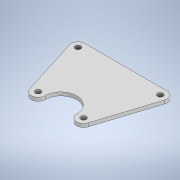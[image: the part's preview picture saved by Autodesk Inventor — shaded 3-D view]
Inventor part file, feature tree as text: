
AUTODESK INVENTOR PART (.ipt)
format: ipt  version: 2020 (Build 240168000, 168)  size: 121,856 bytes
history: native  units: in
note: dims shown in document units (in); Inventor stores cm internally (conversion verified against a paired STEP export)
features: extrude x1, sketch x1
ambient origin geometry x8: Origin, YZ Plane, XZ Plane, XY Plane, X Axis, Y Axis, Z Axis, Center Point
bodies: Solid1 (feature_tree)
feature tree (2):
  extrude  "Extrusion1"  Depth=0.0787in
  sketch  "Sketch1"  dims[d0=1.8898in d1=1.3386in d2=0.5217in d3=0.126in d4=0.126in d5=0.315in d6=0.315in d8=0.0787in d9=0.0in]
